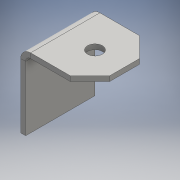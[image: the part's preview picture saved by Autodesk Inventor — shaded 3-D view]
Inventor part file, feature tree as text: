
AUTODESK INVENTOR PART (.ipt)
format: ipt  version: 2016 (Build 200138000, 138)  size: 107,520 bytes
history: native  units: in
note: dims shown in document units (in); Inventor stores cm internally (conversion verified against a paired STEP export)
features: other x3, sketch x3
ambient origin geometry x8: Origin, YZ Plane, XZ Plane, XY Plane, X Axis, Y Axis, Z Axis, Center Point
bodies: Solid1 (feature_tree)
feature tree (6):
  other  "Part120_MIR.ipt"
  other  "Solid1::Part120_MIR.ipt"
  other  "TaggingFeature1"
  sketch  "Sketch1"  dims[d0=0.3937in]
  sketch  "Sketch2"
  sketch  "Sketch3"
